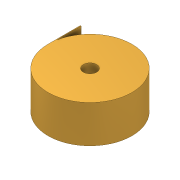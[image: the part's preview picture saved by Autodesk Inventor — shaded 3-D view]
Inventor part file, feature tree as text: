
AUTODESK INVENTOR PART (.ipt)
format: ipt  version: 2021.3 (Build 253353000, 353)  size: 103,424 bytes
history: native  units: mm
features: sketch x2, extrude x1, hole x1
ambient origin geometry x8: Origin, YZ Plane, XZ Plane, XY Plane, X Axis, Y Axis, Z Axis, Center Point
bodies: Solid1 (feature_tree)
feature tree (4):
  extrude  "Extrusion1"  Depth=5.0mm
  hole  "Hole1"  [1 undecoded]
  sketch  "Sketch1"  dims[d0=31.25mm d1=5.0mm]
  sketch  "Sketch2"  dims[d2=14.0mm d3=0.0mm d4=0.3mm d5=12.0mm d6=6.15mm d7=6.0mm d8=10.0mm d9=12.0mm d10=90.0deg d11=8.0mm d12=0.0mm]
note: 1 required parameter value undecoded (feature->parameter linkage not recoverable at this tier; creation-order binding heuristic only, values carry confidence <= 0.55)
